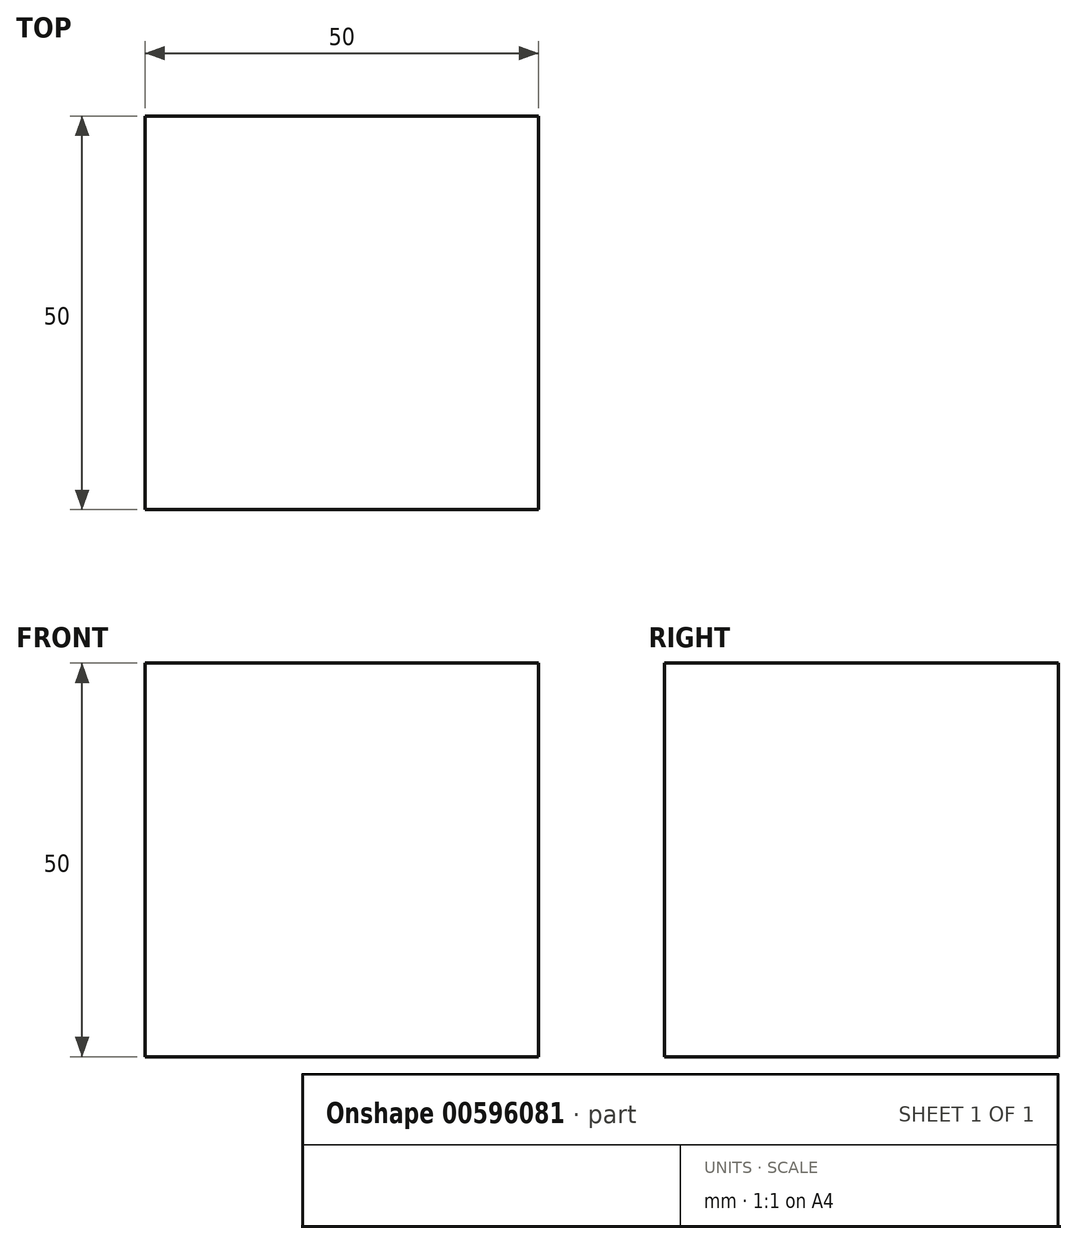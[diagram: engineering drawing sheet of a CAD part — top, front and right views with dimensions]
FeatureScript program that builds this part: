
annotation { "Feature Type Name" : "Feature", "Feature Type Description" : "" }
export const myFeature = defineFeature(function(context is Context, id is Id, definition is map)
    precondition{}
    {
        {
            var Q0;
            Q0=qCreatedBy(makeId("Top.planeOp"),FACE);
            var sketch = newSketch(context, id + "F0", { "sketchPlane" : qUnion([Q0])});
            skLineSegment(sketch, "E0.bottom", {"start": v(25, 25) * mm, "end": v(-25, 25) * mm});
            skLineSegment(sketch, "E0.top", {"start": v(25, -25) * mm, "end": v(-25, -25) * mm});
            skLineSegment(sketch, "E0.left", {"start": v(25, 25) * mm, "end": v(25, -25) * mm});
            skLineSegment(sketch, "E0.right", {"start": v(-25, 25) * mm, "end": v(-25, -25) * mm});
            skPoint(sketch, "E0.middle", {"position": v(0, 0) * mm});
            skSolve(sketch);
        }
        {
            var Q0;
            Q0 = qSketchRegion(id + "F0", true);
            extrude(context, id + "F1", {"entities" : qUnion([Q0]), "depth" : 50 * mm, "offsetDistance" : 25 * mm});
        }
    });
